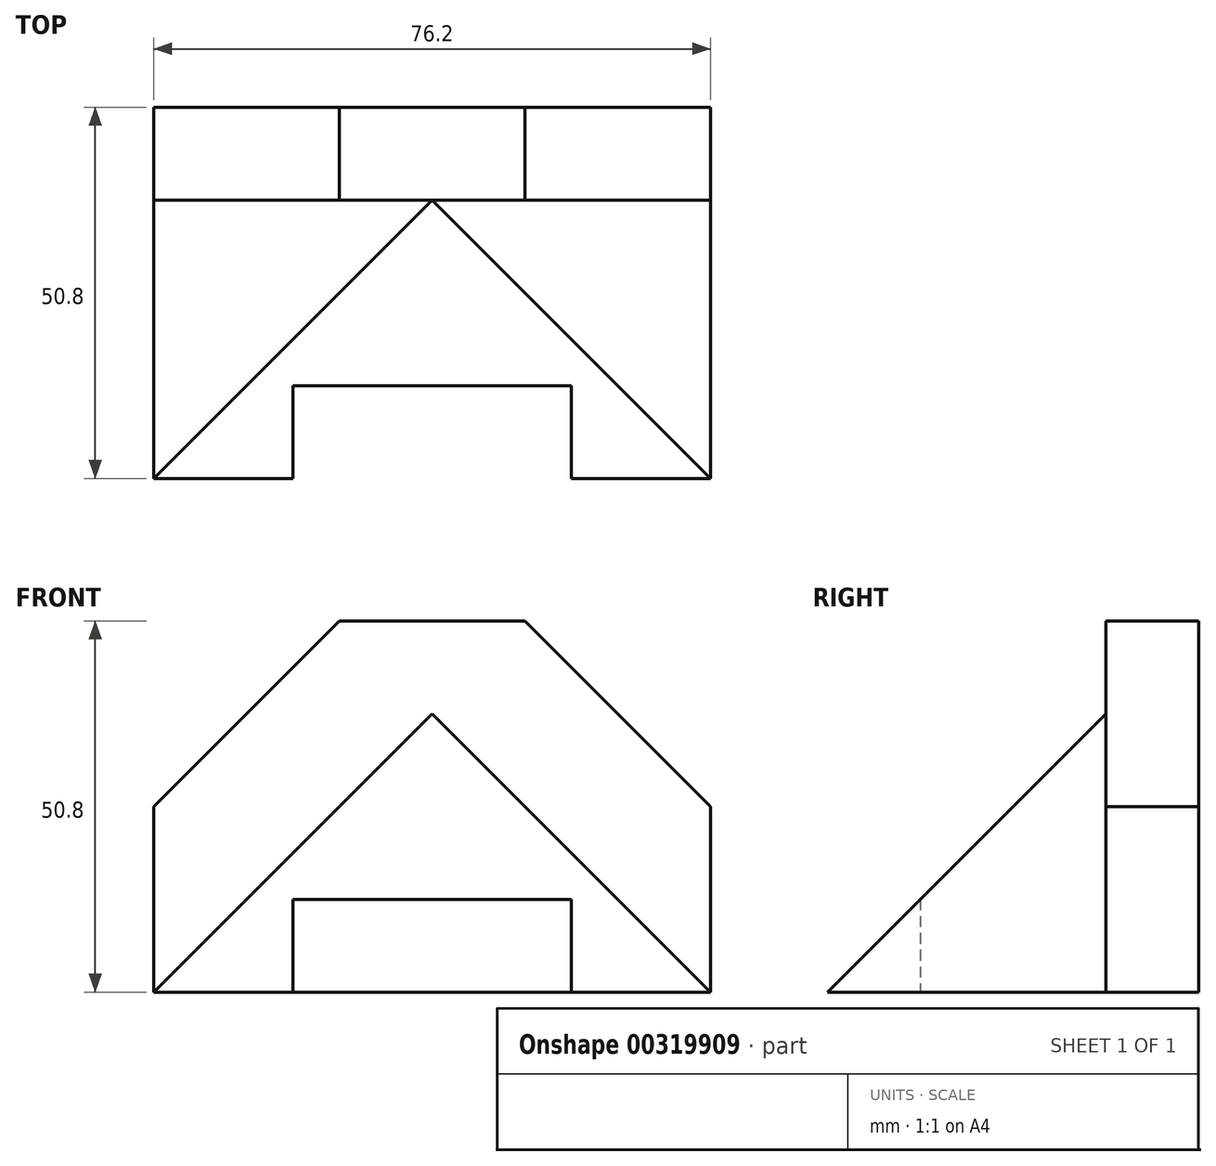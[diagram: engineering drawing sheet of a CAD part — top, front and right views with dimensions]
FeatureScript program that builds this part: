
annotation { "Feature Type Name" : "Feature", "Feature Type Description" : "" }
export const myFeature = defineFeature(function(context is Context, id is Id, definition is map)
    precondition{}
    {
        {
            var Q0;
            Q0=qCreatedBy(makeId("Front.planeOp"),FACE);
            var sketch = newSketch(context, id + "F0", { "sketchPlane" : qUnion([Q0])});
            skLineSegment(sketch, "E0", {"start": v(-38.1, 0) * mm, "end": v(38.1, 0) * mm});
            skLineSegment(sketch, "E1", {"start": v(-38.1, 0) * mm, "end": v(-38.1, 25.4) * mm});
            skLineSegment(sketch, "E2", {"start": v(-38.1, 25.4) * mm, "end": v(-12.7, 50.8) * mm});
            skLineSegment(sketch, "E3", {"start": v(-12.7, 50.8) * mm, "end": v(12.7, 50.8) * mm});
            skLineSegment(sketch, "E4", {"start": v(12.7, 50.8) * mm, "end": v(38.1, 25.4) * mm});
            skLineSegment(sketch, "E5", {"start": v(38.1, 25.4) * mm, "end": v(38.1, 0) * mm});
            skSolve(sketch);
        }
        {
            var Q0;
            Q0 = qSketchRegion(id + "F0", true);
            extrude(context, id + "F1", {"entities" : qUnion([Q0]), "depth" : 12.7 * mm});
        }
        {
            var Q0;
            Q0=makeQuery(id+"F1.opExtrude","CAP_FACE",FACE,{"disambiguationData":[OSD([sQuery(id+"F0.wireOp",EDGE,"E0"),sQuery(id+"F0.wireOp",EDGE,"E1"),sQuery(id+"F0.wireOp",EDGE,"E2"),sQuery(id+"F0.wireOp",EDGE,"E3"),sQuery(id+"F0.wireOp",EDGE,"E4"),sQuery(id+"F0.wireOp",EDGE,"E5")])],"isStart":false});
            var sketch = newSketch(context, id + "F2", { "sketchPlane" : qUnion([Q0])});
            skLineSegment(sketch, "E6", {"start": v(-38.1, 0) * mm, "end": v(38.1, 0) * mm});
            skLineSegment(sketch, "E7", {"start": v(38.1, 0) * mm, "end": v(0, 38.1) * mm});
            skLineSegment(sketch, "E8", {"start": v(0, 38.1) * mm, "end": v(-38.1, 0) * mm});
            skSolve(sketch);
        }
        {
            var Q0;
            Q0 = qSketchRegion(id + "F2", true);
            extrude(context, id + "F3", {"entities" : qUnion([Q0]), "operationType" : NewBodyOperationType.ADD, "depth" : 38.1 * mm});
        }
        {
            var Q0;
            Q0=qCreatedBy(makeId("Right.planeOp"),FACE);
            var sketch = newSketch(context, id + "F4", { "sketchPlane" : qUnion([Q0])});
            skLineSegment(sketch, "E9.0", {"start": v(-50.8, 38.1) * mm, "end": v(-12.7, 38.1) * mm});
            skLineSegment(sketch, "E10.0", {"start": v(-50.8, 38.1) * mm, "end": v(-50.8, 0) * mm});
            skLineSegment(sketch, "E11", {"start": v(-50.8, 0) * mm, "end": v(-12.7, 38.1) * mm});
            skSolve(sketch);
        }
        {
            var Q0;
            Q0 = qSketchRegion(id + "F4", true);
            extrude(context, id + "F5", {"entities" : qUnion([Q0]), "operationType" : NewBodyOperationType.REMOVE, "endBound" : BoundingType.SYMMETRIC, "oppositeDirection" : true, "depth" : 76.2 * mm});
        }
        {
            var Q0;
            Q0=qCreatedBy(makeId("Top.planeOp"),FACE);
            var sketch = newSketch(context, id + "F6", { "sketchPlane" : qUnion([Q0])});
            skLineSegment(sketch, "E12", {"start": v(19.05, -50.8) * mm, "end": v(-19.05, -50.8) * mm});
            skLineSegment(sketch, "E13", {"start": v(-19.05, -50.8) * mm, "end": v(-19.05, -38.1) * mm});
            skLineSegment(sketch, "E14", {"start": v(-19.05, -38.1) * mm, "end": v(19.05, -38.1) * mm});
            skLineSegment(sketch, "E15", {"start": v(19.05, -38.1) * mm, "end": v(19.05, -50.8) * mm});
            skSolve(sketch);
        }
        {
            var Q0;
            Q0 = qSketchRegion(id + "F6", true);
            extrude(context, id + "F7", {"entities" : qUnion([Q0]), "operationType" : NewBodyOperationType.REMOVE, "depth" : 25.4 * mm});
        }
    });
